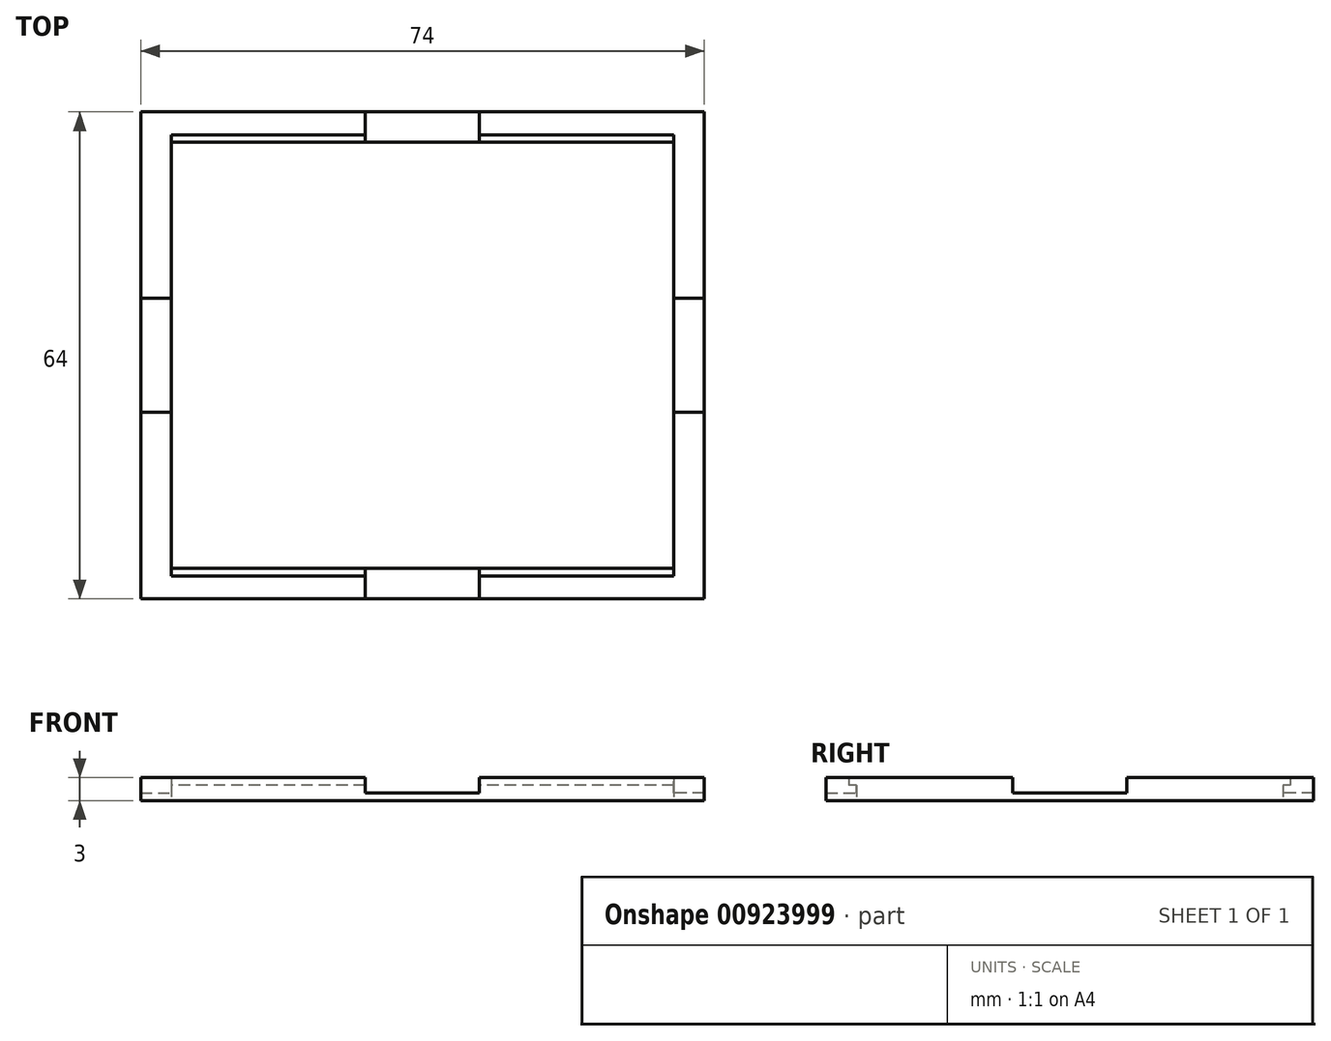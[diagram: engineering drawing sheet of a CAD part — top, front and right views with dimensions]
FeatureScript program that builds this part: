
annotation { "Feature Type Name" : "Feature", "Feature Type Description" : "" }
export const myFeature = defineFeature(function(context is Context, id is Id, definition is map)
    precondition{}
    {
        {
            var Q0;
            Q0=qCreatedBy(makeId("Top.planeOp"),FACE);
            var sketch = newSketch(context, id + "F0", { "sketchPlane" : qUnion([Q0])});
            skLineSegment(sketch, "E0.bottom", {"start": v(0, 0) * mm, "end": v(-68, 0) * mm});
            skLineSegment(sketch, "E0.top", {"start": v(0, -58) * mm, "end": v(-68, -58) * mm});
            skLineSegment(sketch, "E0.left", {"start": v(0, 0) * mm, "end": v(0, -58) * mm});
            skLineSegment(sketch, "E0.right", {"start": v(-68, 0) * mm, "end": v(-68, -58) * mm});
            skLineSegment(sketch, "E1.0", {"start": v(-71, 3) * mm, "end": v(-71, -61) * mm});
            skLineSegment(sketch, "E1.1", {"start": v(3, 3) * mm, "end": v(-71, 3) * mm});
            skLineSegment(sketch, "E1.2", {"start": v(3, 3) * mm, "end": v(3, -61) * mm});
            skLineSegment(sketch, "E1.3", {"start": v(3, -61) * mm, "end": v(-71, -61) * mm});
            skLineSegment(sketch, "E2.0", {"start": v(-1, -1) * mm, "end": v(-67, -1) * mm});
            skLineSegment(sketch, "E2.1", {"start": v(-1, -1) * mm, "end": v(-1, -57) * mm});
            skLineSegment(sketch, "E2.2", {"start": v(-1, -57) * mm, "end": v(-67, -57) * mm});
            skLineSegment(sketch, "E2.3", {"start": v(-67, -1) * mm, "end": v(-67, -57) * mm});
            skSolve(sketch);
        }
        {
            var Q0;
            Q0=makeQuery(id+"F0.imprint","IMPRINT",FACE,{"disambiguationData":[TD([[makeQuery(id+"F0.imprint","IMPRINT",EDGE,{"derivedFrom":sQuery(id+"F0.wireOp",EDGE,"E0.bottom")}),1.0]])]});
            var Q1;
            Q1=makeQuery(id+"F0.imprint","IMPRINT",FACE,{"disambiguationData":[TD([[makeQuery(id+"F0.imprint","IMPRINT",EDGE,{"derivedFrom":sQuery(id+"F0.wireOp",EDGE,"E0.bottom")}),-1.0]])]});
            extrude(context, id + "F1", {"entities" : qUnion([Q0, Q1]), "depth" : 2 * mm, "offsetDistance" : 25 * mm});
        }
        {
            var Q0;
            Q0=makeQuery(id+"F1.opExtrude","CAP_FACE",FACE,{"disambiguationData":[OSD([sQuery(id+"F0.wireOp",EDGE,"E1.0"),sQuery(id+"F0.wireOp",EDGE,"E1.1"),sQuery(id+"F0.wireOp",EDGE,"E1.2"),sQuery(id+"F0.wireOp",EDGE,"E1.3"),sQuery(id+"F0.wireOp",EDGE,"E2.0"),sQuery(id+"F0.wireOp",EDGE,"E2.1"),sQuery(id+"F0.wireOp",EDGE,"E2.2"),sQuery(id+"F0.wireOp",EDGE,"E2.3")])],"isStart":false});
            var sketch = newSketch(context, id + "F2", { "sketchPlane" : qUnion([Q0])});
            skLineSegment(sketch, "E3.bottom", {"start": v(-1, 0) * mm, "end": v(-67, 0) * mm});
            skLineSegment(sketch, "E3.top", {"start": v(-1, -58) * mm, "end": v(-67, -58) * mm});
            skLineSegment(sketch, "E3.left", {"start": v(-1, 0) * mm, "end": v(-1, -58) * mm});
            skLineSegment(sketch, "E3.right", {"start": v(-67, 0) * mm, "end": v(-67, -58) * mm});
            skSolve(sketch);
        }
        {
            var Q0;
            Q0=makeQuery(id+"F2.imprint","IMPRINT",FACE,{"disambiguationData":[TD([[makeQuery(id+"F2.imprint","IMPRINT",EDGE,{"derivedFrom":sQuery(id+"F2.wireOp",EDGE,"E3.bottom")}),-1.0]])]});
            extrude(context, id + "F3", {"entities" : qUnion([Q0]), "operationType" : NewBodyOperationType.ADD, "depth" : 1 * mm, "offsetDistance" : 25 * mm});
        }
        {
            var Q0;
            Q0=makeQuery(id+"F3.opExtrude","CAP_FACE",FACE,{"disambiguationData":[OSD([sQuery(id+"F0.wireOp",EDGE,"E1.0"),sQuery(id+"F0.wireOp",EDGE,"E1.1"),sQuery(id+"F0.wireOp",EDGE,"E1.2"),sQuery(id+"F0.wireOp",EDGE,"E1.3"),sQuery(id+"F2.wireOp",EDGE,"E3.bottom"),sQuery(id+"F2.wireOp",EDGE,"E3.top"),sQuery(id+"F2.wireOp",EDGE,"E3.left"),sQuery(id+"F2.wireOp",EDGE,"E3.right")])],"isStart":false});
            var sketch = newSketch(context, id + "F4", { "sketchPlane" : qUnion([Q0])});
            skLineSegment(sketch, "E4.bottom", {"start": v(-41.5, 9.56) * mm, "end": v(-26.5, 9.56) * mm});
            skLineSegment(sketch, "E4.top", {"start": v(-41.5, -6.15) * mm, "end": v(-26.5, -6.15) * mm});
            skLineSegment(sketch, "E4.left", {"start": v(-41.5, 9.56) * mm, "end": v(-41.5, -6.15) * mm});
            skLineSegment(sketch, "E4.right", {"start": v(-26.5, 9.56) * mm, "end": v(-26.5, -6.15) * mm});
            skLineSegment(sketch, "E5", {"start": v(-34, 0) * mm, "end": v(-34, -58) * mm, "construction": true});
            skLineSegment(sketch, "E6", {"start": v(-67, -29) * mm, "end": v(-1, -29) * mm, "construction": true});
            skPoint(sketch, "E7", {"position": v(-34, -6.15) * mm});
            skLineSegment(sketch, "E8.1.0", {"start": v(-56.85, -36.5) * mm, "end": v(-56.85, -21.5) * mm});
            skLineSegment(sketch, "E8.1.1", {"start": v(-72.56, -21.5) * mm, "end": v(-56.85, -21.5) * mm});
            skLineSegment(sketch, "E8.1.2", {"start": v(-72.56, -36.5) * mm, "end": v(-72.56, -21.5) * mm});
            skLineSegment(sketch, "E8.1.3", {"start": v(-72.56, -36.5) * mm, "end": v(-56.85, -36.5) * mm});
            skLineSegment(sketch, "E8.2.0", {"start": v(-26.5, -51.85) * mm, "end": v(-41.5, -51.85) * mm});
            skLineSegment(sketch, "E8.2.1", {"start": v(-41.5, -67.56) * mm, "end": v(-41.5, -51.85) * mm});
            skLineSegment(sketch, "E8.2.2", {"start": v(-26.5, -67.56) * mm, "end": v(-41.5, -67.56) * mm});
            skLineSegment(sketch, "E8.2.3", {"start": v(-26.5, -67.56) * mm, "end": v(-26.5, -51.85) * mm});
            skLineSegment(sketch, "E8.3.0", {"start": v(-11.15, -21.5) * mm, "end": v(-11.15, -36.5) * mm});
            skLineSegment(sketch, "E8.3.1", {"start": v(4.56, -36.5) * mm, "end": v(-11.15, -36.5) * mm});
            skLineSegment(sketch, "E8.3.2", {"start": v(4.56, -21.5) * mm, "end": v(4.56, -36.5) * mm});
            skLineSegment(sketch, "E8.3.3", {"start": v(4.56, -21.5) * mm, "end": v(-11.15, -21.5) * mm});
            skPoint(sketch, "E8.center", {"position": v(-34, -29) * mm});
            skSolve(sketch);
        }
        {
            var Q0;
            {var subQ0=sQuery(id+"F4.wireOp",EDGE,"E4.bottom");Q0=makeQuery(id+"F4.imprint","IMPRINT",FACE,{"disambiguationData":[TD([[makeQuery(id+"F4.imprint","IMPRINT",EDGE,{"derivedFrom":subQ0}),-1.0]])]});}
            var Q1;
            {var subQ0=sQuery(id+"F4.wireOp",EDGE,"E4.left");var subQ1=makeQuery(id+"F3.opExtrude","CAP_EDGE",EDGE,{"disambiguationData":[OSD([sQuery(id+"F0.wireOp",EDGE,"E1.1")])],"isStart":false});var subQ2=makeQuery(id+"F4.imprint","INTERSECT",VERTEX,{"derivedFrom":[subQ1,subQ0]});Q1=makeQuery(id+"F4.imprint","IMPRINT",FACE,{"disambiguationData":[TD([[makeQuery(id+"F4.imprint","IMPRINT",EDGE,{"disambiguationData":[TD([[subQ2,-1.0]])],"derivedFrom":subQ0}),1.0]])]});}
            var Q2;
            {var subQ0=sQuery(id+"F4.wireOp",EDGE,"E4.top");Q2=makeQuery(id+"F4.imprint","IMPRINT",FACE,{"disambiguationData":[TD([[makeQuery(id+"F4.imprint","IMPRINT",EDGE,{"derivedFrom":subQ0}),1.0]])]});}
            var Q3;
            {var subQ0=sQuery(id+"F4.wireOp",EDGE,"E8.3.1");var subQ1=makeQuery(id+"F3.opExtrude","CAP_EDGE",EDGE,{"disambiguationData":[OSD([sQuery(id+"F0.wireOp",EDGE,"E1.2")])],"isStart":false});var subQ2=makeQuery(id+"F4.imprint","INTERSECT",VERTEX,{"derivedFrom":[subQ1,subQ0]});Q3=makeQuery(id+"F4.imprint","IMPRINT",FACE,{"disambiguationData":[TD([[makeQuery(id+"F4.imprint","IMPRINT",EDGE,{"disambiguationData":[TD([[subQ2,-1.0]])],"derivedFrom":subQ0}),-1.0]])]});}
            var Q4;
            {var subQ0=sQuery(id+"F4.wireOp",EDGE,"E8.3.2");Q4=makeQuery(id+"F4.imprint","IMPRINT",FACE,{"disambiguationData":[TD([[makeQuery(id+"F4.imprint","IMPRINT",EDGE,{"derivedFrom":subQ0}),-1.0]])]});}
            var Q5;
            {var subQ0=sQuery(id+"F4.wireOp",EDGE,"E8.3.0");Q5=makeQuery(id+"F4.imprint","IMPRINT",FACE,{"disambiguationData":[TD([[makeQuery(id+"F4.imprint","IMPRINT",EDGE,{"derivedFrom":subQ0}),1.0]])]});}
            var Q6;
            {var subQ0=sQuery(id+"F4.wireOp",EDGE,"E8.2.1");var subQ1=makeQuery(id+"F3.opExtrude","CAP_EDGE",EDGE,{"disambiguationData":[OSD([sQuery(id+"F0.wireOp",EDGE,"E1.3")])],"isStart":false});var subQ2=makeQuery(id+"F4.imprint","INTERSECT",VERTEX,{"derivedFrom":[subQ1,subQ0]});Q6=makeQuery(id+"F4.imprint","IMPRINT",FACE,{"disambiguationData":[TD([[makeQuery(id+"F4.imprint","IMPRINT",EDGE,{"disambiguationData":[TD([[subQ2,-1.0]])],"derivedFrom":subQ0}),-1.0]])]});}
            var Q7;
            {var subQ0=sQuery(id+"F4.wireOp",EDGE,"E8.2.0");Q7=makeQuery(id+"F4.imprint","IMPRINT",FACE,{"disambiguationData":[TD([[makeQuery(id+"F4.imprint","IMPRINT",EDGE,{"derivedFrom":subQ0}),1.0]])]});}
            var Q8;
            {var subQ0=sQuery(id+"F4.wireOp",EDGE,"E8.2.2");Q8=makeQuery(id+"F4.imprint","IMPRINT",FACE,{"disambiguationData":[TD([[makeQuery(id+"F4.imprint","IMPRINT",EDGE,{"derivedFrom":subQ0}),-1.0]])]});}
            var Q9;
            {var subQ0=sQuery(id+"F4.wireOp",EDGE,"E8.1.0");Q9=makeQuery(id+"F4.imprint","IMPRINT",FACE,{"disambiguationData":[TD([[makeQuery(id+"F4.imprint","IMPRINT",EDGE,{"derivedFrom":subQ0}),1.0]])]});}
            var Q10;
            {var subQ0=sQuery(id+"F4.wireOp",EDGE,"E8.1.1");var subQ1=makeQuery(id+"F3.opExtrude","CAP_EDGE",EDGE,{"disambiguationData":[OSD([sQuery(id+"F0.wireOp",EDGE,"E1.0")])],"isStart":false});var subQ2=makeQuery(id+"F4.imprint","INTERSECT",VERTEX,{"derivedFrom":[subQ1,subQ0]});Q10=makeQuery(id+"F4.imprint","IMPRINT",FACE,{"disambiguationData":[TD([[makeQuery(id+"F4.imprint","IMPRINT",EDGE,{"disambiguationData":[TD([[subQ2,-1.0]])],"derivedFrom":subQ0}),-1.0]])]});}
            var Q11;
            {var subQ0=sQuery(id+"F4.wireOp",EDGE,"E8.1.2");Q11=makeQuery(id+"F4.imprint","IMPRINT",FACE,{"disambiguationData":[TD([[makeQuery(id+"F4.imprint","IMPRINT",EDGE,{"derivedFrom":subQ0}),-1.0]])]});}
            extrude(context, id + "F5", {"entities" : qUnion([Q0, Q1, Q2, Q3, Q4, Q5, Q6, Q7, Q8, Q9, Q10, Q11]), "operationType" : NewBodyOperationType.REMOVE, "oppositeDirection" : true, "depth" : 2 * mm, "offsetDistance" : 25 * mm});
        }
    });
